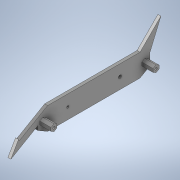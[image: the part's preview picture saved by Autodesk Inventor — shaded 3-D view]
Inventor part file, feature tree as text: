
AUTODESK INVENTOR PART (.ipt)
format: ipt  version: 2020 (Build 240168000, 168)  size: 182,784 bytes
history: native  units: in
note: dims shown in document units (in); Inventor stores cm internally (conversion verified against a paired STEP export)
features: other x3, extrude x2, sketch x2
ambient origin geometry x8: Origin, YZ Plane, XZ Plane, XY Plane, X Axis, Y Axis, Z Axis, Center Point
bodies: Solid1 (feature_tree)
feature tree (7):
  other  "HexWheelGuard.ipt"
  extrude  "Extrusion1"  TaperAngle=0.0deg  [1 undecoded]
  extrude  "Extrusion2"  Depth=0.5906in
  other  "Solid1::HexWheelGuard.ipt"
  other  "TaggingFeature1"
  sketch  "Sketch1"  dims[d0=0.3937in d6=0.0in d7=0.0in]
  sketch  "Sketch2"  dims[d9=0.315in d10=1.4843in d11=60.0deg d12=0.0787in d13=0.3937in d14=0.0in d20=0.3937in d21=0.5906in d22=1.1024in]
note: 1 required parameter value undecoded (feature->parameter linkage not recoverable at this tier; creation-order binding heuristic only, values carry confidence <= 0.55)
